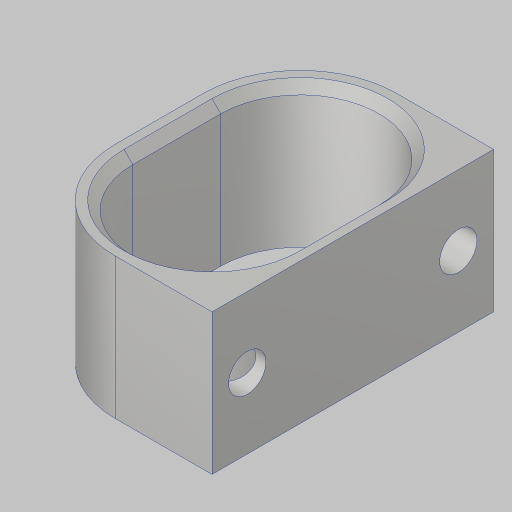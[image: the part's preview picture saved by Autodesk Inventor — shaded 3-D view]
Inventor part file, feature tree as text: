
AUTODESK INVENTOR PART (.ipt)
format: ipt  version: 2023.5 (Build 275446000, 446)  size: 170,496 bytes
history: native  units: in
note: dims shown in document units (in); Inventor stores cm internally (conversion verified against a paired STEP export)
features: extrude x3, projected_geometry x3, sketch x2, chamfer x1
ambient origin geometry x8: Origin, YZ Plane, XZ Plane, XY Plane, X Axis, Y Axis, Z Axis, Center Point
bodies: Solid1 (feature_tree)
feature tree (9):
  sketch  "Sketch1"  dims[d1=1.375in d2=0.125in]
  extrude  "Extrusion1"  Depth=0.125in
  extrude  "Extrusion2"  Depth=1.0in TaperAngle=0.0deg
  extrude  "Extrusion3"  Depth=0.125in
  chamfer  "Chamfer1"  Distance=1.5in
  sketch  "Sketch2"  dims[d3=2.0in d4=1.0in d5=0.0in d6=0.2657in d7=1.5in d8=1.0in d9=0.0in d10=1.0in d11=0.0in d12=0.0625in d13=0.125in d14=45.0deg]
  projected_geometry  "Projected Loop1"
  projected_geometry  "Projected Loop2"
  projected_geometry  "Projected Loop3"
